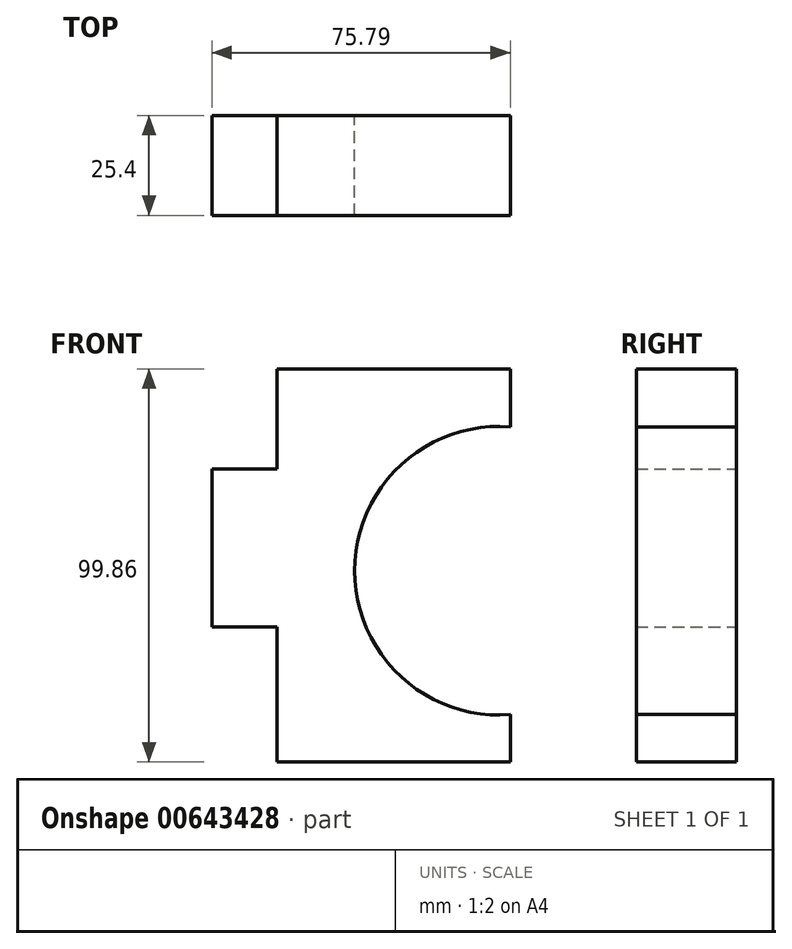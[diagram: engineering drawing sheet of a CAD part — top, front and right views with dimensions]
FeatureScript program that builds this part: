
annotation { "Feature Type Name" : "Feature", "Feature Type Description" : "" }
export const myFeature = defineFeature(function(context is Context, id is Id, definition is map)
    precondition{}
    {
        {
            var Q0;
            Q0=qCreatedBy(makeId("Front.planeOp"),FACE);
            var sketch = newSketch(context, id + "F0", { "sketchPlane" : qUnion([Q0])});
            skLineSegment(sketch, "E0", {"start": v(-121.93, -47.03) * mm, "end": v(-62.64, -47.03) * mm});
            skLineSegment(sketch, "E1", {"start": v(-62.64, -47.03) * mm, "end": v(-62.64, -35) * mm});
            skLineSegment(sketch, "E2", {"start": v(-62.64, 38.12) * mm, "end": v(-62.64, 52.83) * mm});
            skLineSegment(sketch, "E3", {"start": v(-62.64, 52.83) * mm, "end": v(-121.93, 52.83) * mm});
            skLineSegment(sketch, "E4", {"start": v(-121.93, 52.83) * mm, "end": v(-121.93, 27.42) * mm});
            skLineSegment(sketch, "E5", {"start": v(-121.93, 27.42) * mm, "end": v(-138.43, 27.42) * mm});
            skLineSegment(sketch, "E6", {"start": v(-138.43, 27.42) * mm, "end": v(-138.43, -12.7) * mm});
            skLineSegment(sketch, "E7", {"start": v(-138.43, -12.7) * mm, "end": v(-121.93, -12.7) * mm});
            skLineSegment(sketch, "E8", {"start": v(-121.93, -12.7) * mm, "end": v(-121.93, -47.03) * mm});
            skArc(sketch, "E9", {"start": v(-62.64, 38.12) * mm, "mid": v(-102.17, 1.56) * mm, "end": v(-62.64, -35) * mm});
            skSolve(sketch);
        }
        {
            var Q0;
            Q0 = qSketchRegion(id + "F0", true);
            extrude(context, id + "F1", {"entities" : qUnion([Q0]), "depth" : 25.4 * mm, "offsetDistance" : 25.4 * mm});
        }
    });
